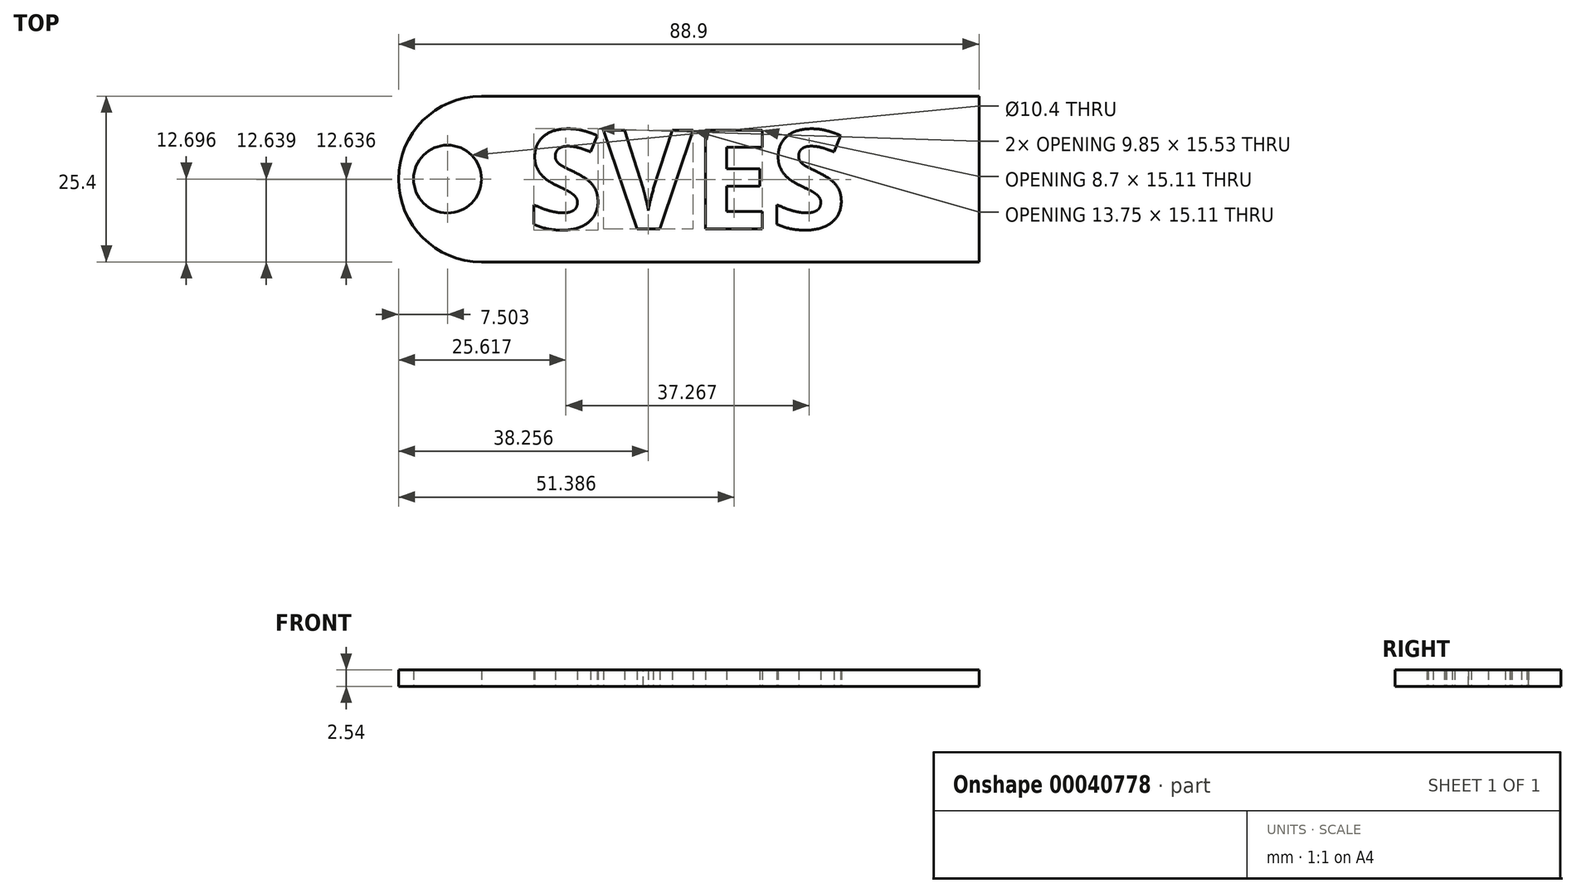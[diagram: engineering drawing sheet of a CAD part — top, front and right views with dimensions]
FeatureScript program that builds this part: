
annotation { "Feature Type Name" : "Feature", "Feature Type Description" : "" }
export const myFeature = defineFeature(function(context is Context, id is Id, definition is map)
    precondition{}
    {
        {
            var Q0;
            Q0=qCreatedBy(makeId("Top.planeOp"),FACE);
            var sketch = newSketch(context, id + "F0", { "sketchPlane" : qUnion([Q0])});
            skText(sketch, "E0", { "text": "SVES", "fontName": "OpenSans-Bold.ttf"});
            skPoint(sketch, "E0.secondSnap0", {"position": v(16.56, -5.56) * mm});
            skLineSegment(sketch, "E1.bottom", {"start": v(-39.36, 14.76) * mm, "end": v(36.84, 14.76) * mm});
            skLineSegment(sketch, "E1.top", {"start": v(-39.36, -10.64) * mm, "end": v(36.84, -10.64) * mm});
            skLineSegment(sketch, "E1.right", {"start": v(36.84, 14.76) * mm, "end": v(36.84, -10.64) * mm});
            skArc(sketch, "E2", {"start": v(-39.36, 14.76) * mm, "mid": v(-52.06, 2.06) * mm, "end": v(-39.36, -10.64) * mm});
            skCircle(sketch, "E3", {"center": v(-44.56, 2.06) * mm, "radius": 5.2 * mm});
            skText(sketch, "E4", { "text": "2016\n", "fontName": "OpenSans-Bold.ttf"});
            const initialGuessF0  = {"E0": [-0.03234, -0.00556, 1, 0, 0.01524], "E4": [-0.00063, 0.05067, 1, 0, 0.00632]};
            skSetInitialGuess(sketch, initialGuessF0);
            skSolve(sketch);
        }
        {
            var Q0;
            Q0=makeQuery(id+"F0.imprint","IMPRINT",FACE,{"disambiguationData":[TD([[makeQuery(id+"F0.imprint","IMPRINT",EDGE,{"derivedFrom":sQuery(id+"F0.wireOp",EDGE,"E0.sketch_text.stroke-0")}),1.0]])]});
            extrude(context, id + "F1", {"entities" : qUnion([Q0]), "depth" : 2.54 * mm});
        }
    });
